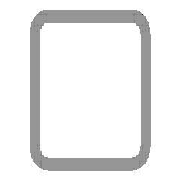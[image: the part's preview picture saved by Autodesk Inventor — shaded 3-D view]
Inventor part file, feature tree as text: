
AUTODESK INVENTOR PART (.ipt)
format: ipt  version: 2021 (Build 250183000, 183)  size: 154,112 bytes
history: native  units: mm (DEFAULTED — no unit token found)
features: other x6, sketch x3, split x2, extrude x1, plane x1
ambient origin geometry x8: Origin, YZ Plane, XZ Plane, XY Plane, X Axis, Y Axis, Z Axis, Center Point
bodies: Solid1 (feature_tree)
feature tree (13):
  parser-record x1  (decoder bookkeeping rows leaked as tree rows — omitted from the tree; the rows remain in map.json)
  other  "Driven Length"
  other  "Plano inicial"
  other  "Plano final"
  extrude  "Corpo"  TaperAngle=0.0deg  [1 undecoded]
  other  "Plano de trabalho4"
  split  "Dividir1"
  other  "Plano de trabalho5"
  split  "Dividir2"
  sketch  "Esboço"  dims[d11=50.8mm d12=4.7625mm d13=-34.077676mm d14=2032.730983mm d15=25.4mm d16=25.4mm d17=9.525mm d18=90.0deg d19=2066.808659mm]
  sketch  "Sketch3"  dims[d3=2060.382021mm d4=0.0mm]
  plane  "Work Plane3"
  sketch  "Sketch4"  dims[d10=50.8mm]
note: 1 required parameter value undecoded (feature->parameter linkage not recoverable at this tier; creation-order binding heuristic only, values carry confidence <= 0.55)
